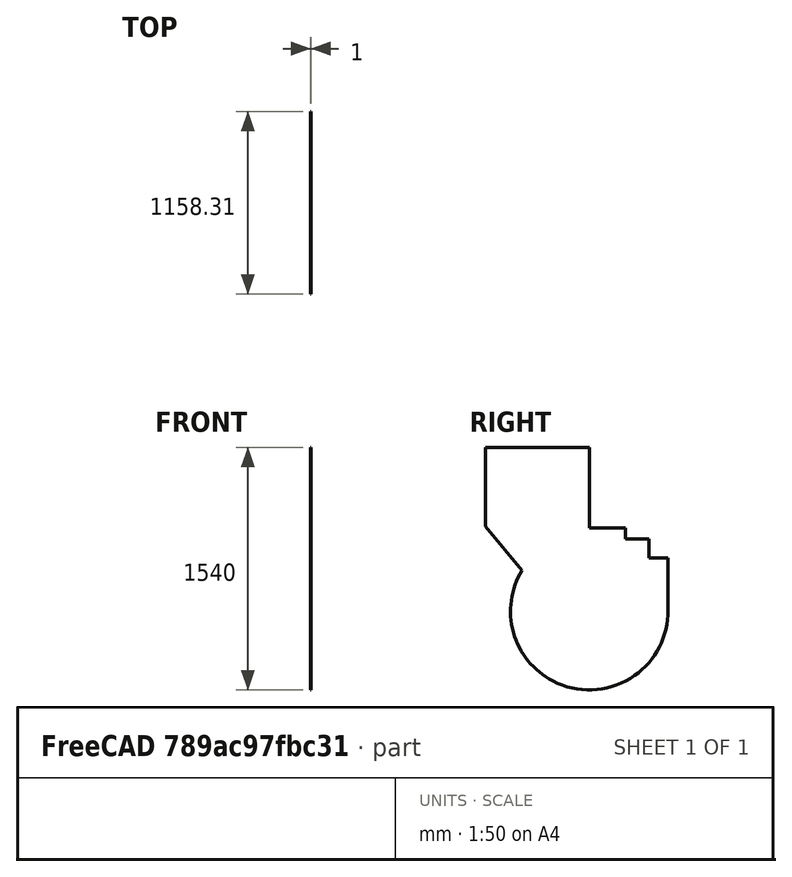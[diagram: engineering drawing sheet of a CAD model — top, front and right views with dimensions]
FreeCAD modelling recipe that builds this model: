
FCSTD DOCUMENT
Label: Shell_back_no_bin
objects: Sketcher::SketchObject×1, PartDesign::Pad×1
note: 3 computed .brp shape members not serialized (recipe doc carries the construction recipe); baked Part::Feature solids carry a one-line shape summary decoded from their .brp

FEATURE [Sketcher::SketchObject] Sketch  label="Shell_back"
  Placement = pos=(-500,0,0) rot=(0.57735,0.57735,0.57735;2.0944rad)
  sketch-geometry (13):
    g0: ArcOfCircle CenterX=0 CenterY=0 CenterZ=0 NormalX=0 NormalY=0 NormalZ=1 Radius=500 StartAngle=2.59474 EndAngle=4.23018
    g1: LineSegment StartX=-427.083 StartY=260 StartZ=0 EndX=-658.874 EndY=540 EndZ=0
    g2: LineSegment StartX=0 StartY=530 StartZ=0 EndX=230 EndY=530 EndZ=0
    g3: LineSegment StartX=230 StartY=530 StartZ=0 EndX=230 EndY=460 EndZ=0
    g4: LineSegment StartX=230 StartY=460 StartZ=0 EndX=380 EndY=460 EndZ=0
    g5: LineSegment StartX=380 StartY=460 StartZ=0 EndX=380 EndY=340 EndZ=0
    g6: LineSegment StartX=380 StartY=340 StartZ=0 EndX=499.438 EndY=340 EndZ=0
    g7: LineSegment StartX=499.438 StartY=340 StartZ=0 EndX=499.438 EndY=-23.6939 EndZ=0
    g8: LineSegment StartX=-658.874 StartY=1040 StartZ=0 EndX=-658.874 EndY=540 EndZ=0
    g9: ArcOfCircle CenterX=0 CenterY=0 CenterZ=0 NormalX=0 NormalY=0 NormalZ=1 Radius=500 StartAngle=5.2631 EndAngle=6.23578
    g10: LineSegment StartX=-658.874 StartY=1040 StartZ=0 EndX=0 EndY=1040 EndZ=0
    g11: LineSegment StartX=0 StartY=1040 StartZ=0 EndX=0 EndY=530 EndZ=0
    g12: ArcOfCircle CenterX=0 CenterY=0 CenterZ=0 NormalX=0 NormalY=0 NormalZ=1 Radius=500 StartAngle=4.23018 EndAngle=5.2631
  constraints (40):
    c: DistanceX(g0) = 0
    c: DistanceY(g0) = 0
    c: Horizontal(g2)
    c: Vertical(g3)
    c: Coincident(g4,g3)
    c: Horizontal(g4)
    c: Vertical(g5)
    c: Coincident(g6,g5)
    c: Horizontal(g6)
    c: DistanceY(g1) = 540
    c: Coincident(g2,g3)
    c: Coincident(g4,g5)
    c: Vertical(g7)
    c: Coincident(g1,g0)
    c: Coincident(g8,g1)
    c: Vertical(g8)
    c: Distance(g1) = 363.493
    c: Distance(g8) = 500
    c: Coincident(g0,g9)
    c: Coincident(g10,g8)
    c: Horizontal(g10)
    c: Coincident(g11,g10)
    c: Vertical(g11)
    c: Coincident(g6,g7)
    c: Coincident(g11,g2)
    c: DistanceX(g5) = 380
    c: DistanceY(g5) = 340
    c: DistanceX(g3) = 230
    c: DistanceY(g3) = 460
    c: DistanceX(g2) = 0
    c: DistanceY(g2) = 530
    c: DistanceY(g0) = 260
    c: Coincident(g9,g7)
    c: Distance(g7) = 363.694
    c: Coincident(g12,g0)
    c: Coincident(g12,g9)
    c: Coincident(g12,g0)
    c: Radius(g12) = 500
    c: DistanceY(g9) = -426.077
    c: DistanceY(g0) = -442.985
FEATURE [PartDesign::Pad] Pad  label="Shell_back_"
  Length = 1
  MirroredExtent = false
  Reversed = true
  Sketch = -> Sketch
